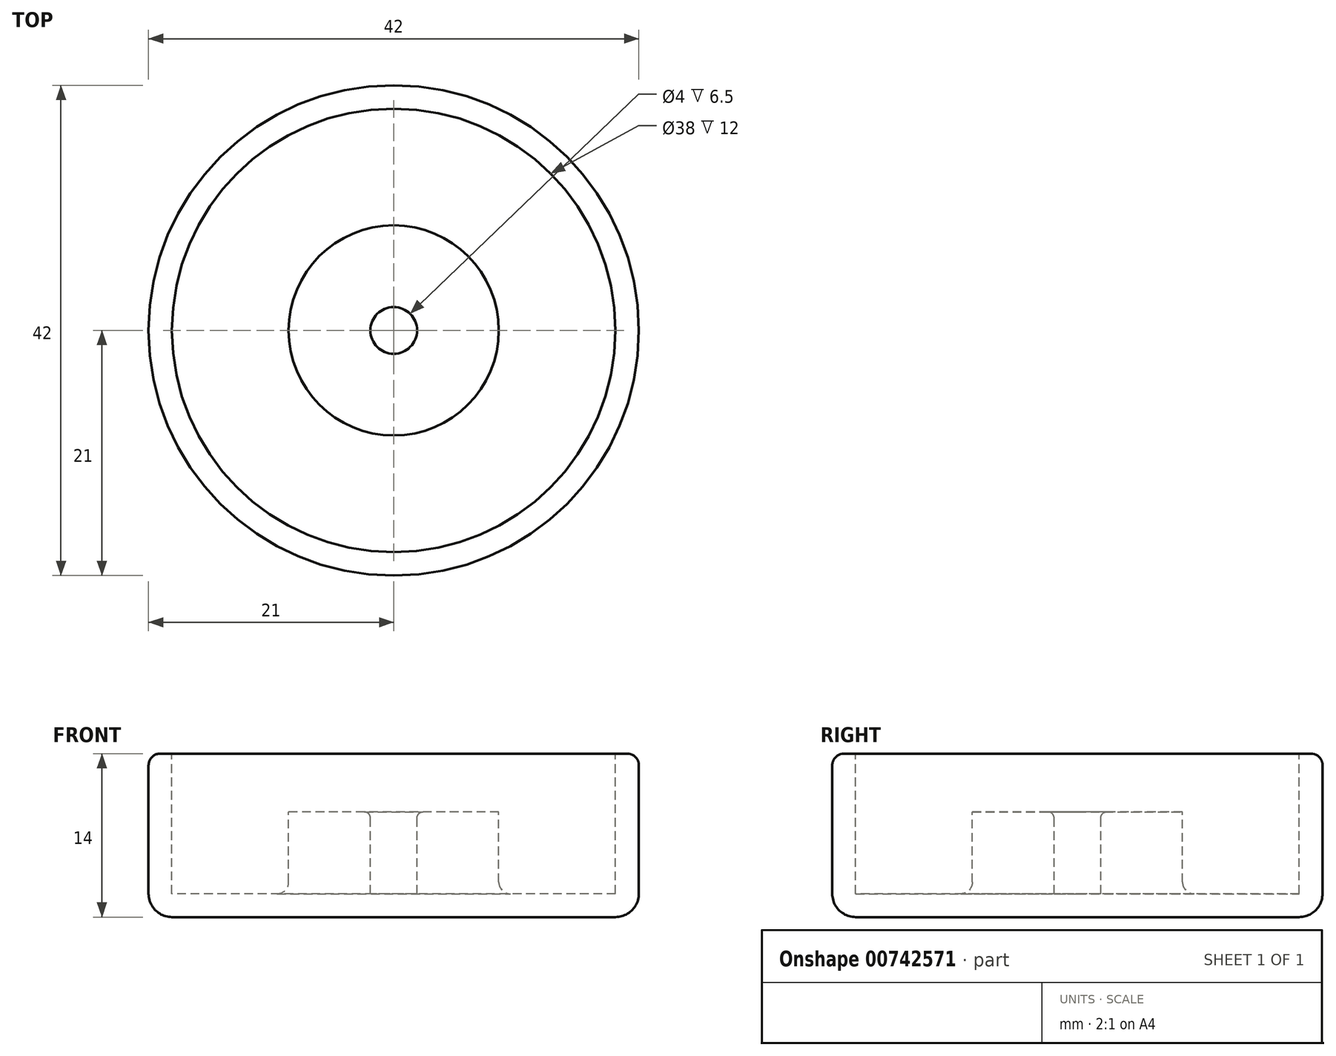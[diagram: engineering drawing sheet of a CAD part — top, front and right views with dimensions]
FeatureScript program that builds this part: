
annotation { "Feature Type Name" : "Feature", "Feature Type Description" : "" }
export const myFeature = defineFeature(function(context is Context, id is Id, definition is map)
    precondition{}
    {
        {
            var Q0;
            Q0=qCreatedBy(makeId("Front.planeOp"),FACE);
            var sketch = newSketch(context, id + "F0", { "sketchPlane" : qUnion([Q0])});
            skLineSegment(sketch, "E0", {"start": v(0, 0) * mm, "end": v(-21, 0) * mm});
            skLineSegment(sketch, "E1", {"start": v(-21, 0) * mm, "end": v(-21, 14) * mm});
            skLineSegment(sketch, "E2", {"start": v(-21, 14) * mm, "end": v(-19, 14) * mm});
            skLineSegment(sketch, "E3", {"start": v(-19, 14) * mm, "end": v(-19, 2) * mm});
            skLineSegment(sketch, "E4", {"start": v(-19, 2) * mm, "end": v(-9, 2) * mm});
            skLineSegment(sketch, "E5", {"start": v(-9, 2) * mm, "end": v(-9, 9) * mm});
            skLineSegment(sketch, "E6", {"start": v(-9, 9) * mm, "end": v(-2, 9) * mm});
            skLineSegment(sketch, "E7", {"start": v(-2, 9) * mm, "end": v(-2, 2) * mm});
            skLineSegment(sketch, "E8", {"start": v(-2, 2) * mm, "end": v(0, 2) * mm});
            skLineSegment(sketch, "E9", {"start": v(0, 2) * mm, "end": v(0, 0) * mm});
            skSolve(sketch);
        }
        {
            var Q0;
            Q0=makeQuery(id+"F0.imprint","IMPRINT",FACE,{"disambiguationData":[TD([[makeQuery(id+"F0.imprint","IMPRINT",EDGE,{"derivedFrom":sQuery(id+"F0.wireOp",EDGE,"E0")}),-1.0]])]});
            var Q1;
            Q1=sQuery(id+"F0.wireOp",EDGE,"E9");
            revolve(context, id + "F1", {"surfaceOperationType" : NewSurfaceOperationType.NEW, "entities" : qUnion([Q0]), "axis" : qUnion([Q1]), "revolveType" : RevolveType.FULL});
        }
        {
            var Q0;
            Q0=makeQuery(id+"F1.opRevolve","SWEPT_EDGE",EDGE,{"disambiguationData":[OSD([sQuery(id+"F0.wireOp",EDGE,"E0"),sQuery(id+"F0.wireOp",EDGE,"E1")])]});
            fillet(context, id + "F2", {"entities" : qUnion([Q0]), "radius" : 2 * mm, "tangentPropagation" : true, "allowEdgeOverflow" : false});
        }
        {
            var Q0;
            Q0=makeQuery(id+"F1.opRevolve","SWEPT_EDGE",EDGE,{"disambiguationData":[OSD([sQuery(id+"F0.wireOp",EDGE,"E1"),sQuery(id+"F0.wireOp",EDGE,"E2")])]});
            fillet(context, id + "F3", {"entities" : qUnion([Q0]), "radius" : 1 * mm, "tangentPropagation" : true, "allowEdgeOverflow" : false});
        }
        {
            var Q0;
            Q0=makeQuery(id+"F1.opRevolve","SWEPT_EDGE",EDGE,{"disambiguationData":[OSD([sQuery(id+"F0.wireOp",EDGE,"E6"),sQuery(id+"F0.wireOp",EDGE,"E7")])]});
            fillet(context, id + "F4", {"entities" : qUnion([Q0]), "radius" : 0.5 * mm, "tangentPropagation" : true, "allowEdgeOverflow" : false});
        }
        {
            var Q0;
            Q0=makeQuery(id+"F1.opRevolve","SWEPT_EDGE",EDGE,{"disambiguationData":[OSD([sQuery(id+"F0.wireOp",EDGE,"E4"),sQuery(id+"F0.wireOp",EDGE,"E5")])]});
            fillet(context, id + "F5", {"entities" : qUnion([Q0]), "radius" : 1 * mm, "tangentPropagation" : true, "allowEdgeOverflow" : false});
        }
    });
